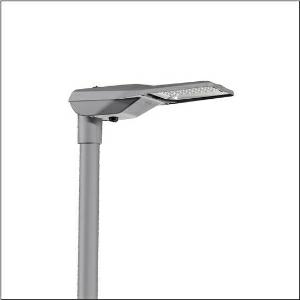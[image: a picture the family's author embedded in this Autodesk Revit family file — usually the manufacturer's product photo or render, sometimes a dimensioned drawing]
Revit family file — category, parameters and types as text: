
# Revit family: streetlight_sl_21_mini___p0_8a_5xe2u33t08gb_af06
name_source: partatom
category: Lighting Fixtures
units: mm (PartAtom-declared; Revit-internal decimal feet)

## family parameters
Cut with Voids When Loaded = No
Host = Face
Light Source = No
Part Type = Normal
Room Calculation Point = No
Round Connector Dimension = Use Diameter
Shared = No

## types (1)
- --- (1 x LED, 5990 lm, 40.4 W, 3000K)
    Apparent Load = 40 VA
    CIE Flux Codes = 33 69 96 100 100
    Color Rendering = 70
    Color Temperature = 3000K
    Default Elevation = 1800 mm
    Description = Streetlight SL 21 mini, mast luminaire, primary light control with lens, of PMMA, primary optical cover: cover, of toughened safety glass, transparent, light distribution: P0.8a, light emission: direct distribution, primary light characteristic: asymmetric, installation type: post-top, side-entry, LED, High Power LED, rated luminous flux: 5.990lm, luminous efficacy: 148lm/W, light colour: 730, colour temperature: 3000K, control gear: D4i, control: pre-setting: logarithmic dimming characteristic, flexible luminous flux parameterisation, time-dependent luminous flux control, constant luminous flux control, overheat protection, mains connection: 220..240V, AC, 50/60Hz, start of lifetime: 40W, end of service life: 41W, reduction: 19W, luminaire housing, of diecast aluminium, powder-coated, Siteco® metallic grey (DB 702S), corrosivity category C5 mid according to DIN EN ISO 12944, multi-level sealing system, sealing non-destructively replaceable, inclination adjustable: 0°, 5°, 10°, 15°, please order mast flange separately, length: 628mm, width: 235mm, height: 110mm, mast flange for spigot size: 42mm (side-entry): 5XC10008XM4, 60/48mm (side-entry/post-top): 5XC10108XM2, 76/60mm (side-entry/post-top): 5XC10108XM1, mounting height: 4..8m, Smart Interface below and above, protection rating (complete): IP66, insulation class (complete): insulation class II (safety insulation), certification: CE, ENEC, ENEC+, VDE, impact resistance: IK10, permissible operating ambient temperature for outdoor applications: -40..+50°C, standard-compliant lighting for roads and squares, packaging unit: 1 piece

Light Distribution: P0.8a
    Height = 110 mm
    Lamp = 1 x LED
    Lamp Light Flux = 5990 lm
    Lamp Power = 40.4 W
    Lamp count = 1
    Length = 625 mm
    Luminous efficacy = 148 lm/W
    Manufacturer = Siteco
    ModVariant = No
    Model = 5XE2U33T08GB
    Number of Poles = 1
    OnlyDefault = Yes
    Power Factor = 1
    Product Name = Streetlight SL 21 mini | P0.8a
    Product group = mast luminaire | pylon top
    ProductGroupID = 6100
    Protection Class = Protection class II
    Protection Degree = IP 66
    RLX_Detail_Level = 1
    RLX_Emergency_Light_Flux = 0 lm
    RLX_Emergency_Type = 0
    RLX_Emergency_Type_DB = No
    RlxData = <blob elided: 93129 chars, md5=b880a220>
    Socket = socket
    Standby Power = 0 W
    System Light Flux = 5990 lm
    System Power = 40 W
    Type Comments = factory setting: luminous flux: 100 % | dim-lin: 254 | 812 mA
    Type Image = l_1003514.jpg
    URL = http://relux.com
    VarID = @adj_093735
    Voltage = 0 V
    Weight = 0.00 kg
    Width = 234 mm

## geometry (parser evidence)
native form markers: Blend x4, Sweep x10
no freeform markers — native parametric forms only
